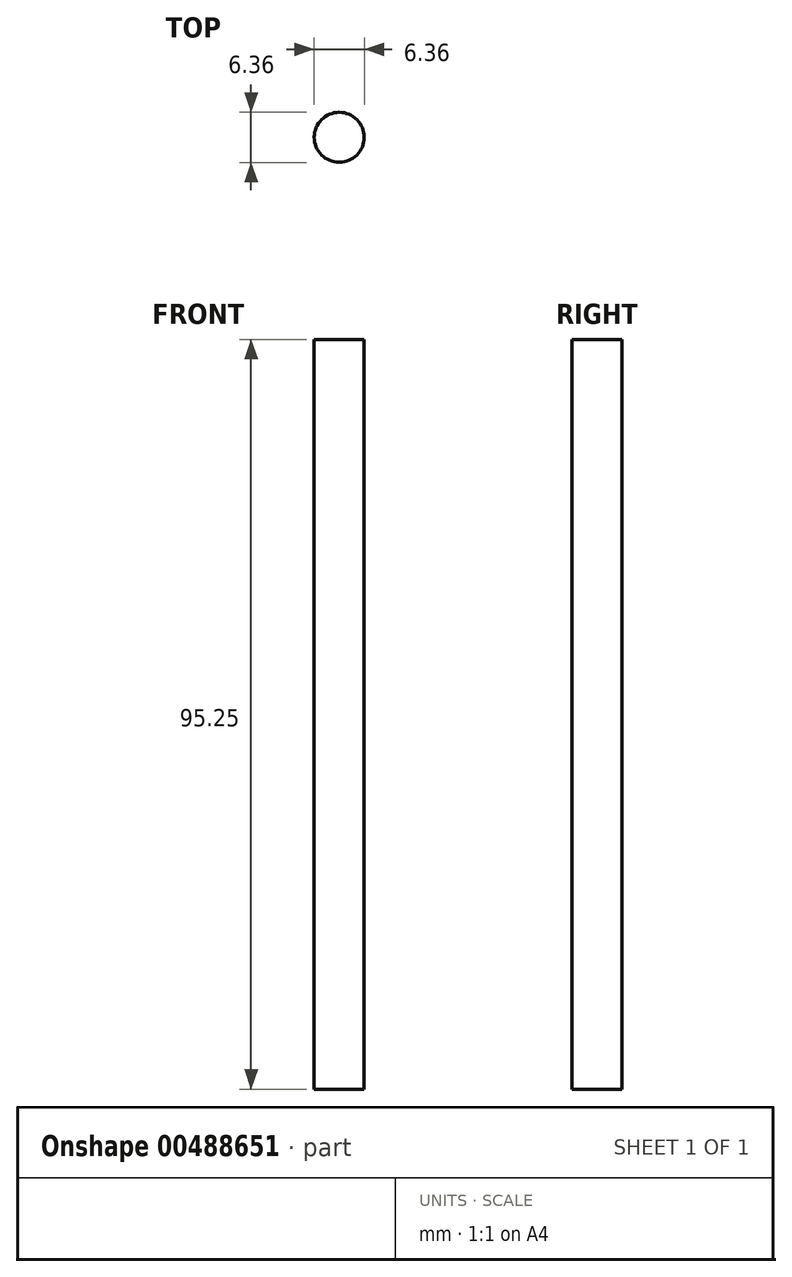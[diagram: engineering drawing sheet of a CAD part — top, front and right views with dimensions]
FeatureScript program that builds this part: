
annotation { "Feature Type Name" : "Feature", "Feature Type Description" : "" }
export const myFeature = defineFeature(function(context is Context, id is Id, definition is map)
    precondition{}
    {
        {
            var Q0;
            Q0=qCreatedBy(makeId("Top.planeOp"),FACE);
            var sketch = newSketch(context, id + "F0", { "sketchPlane" : qUnion([Q0])});
            skCircle(sketch, "E0", {"center": v(0, 0) * mm, "radius": 3.18 * mm});
            skSolve(sketch);
        }
        {
            var Q0;
            Q0=makeQuery(id+"F0.imprint","IMPRINT",FACE,{"disambiguationData":[TD([[makeQuery(id+"F0.imprint","IMPRINT",EDGE,{"derivedFrom":sQuery(id+"F0.wireOp",EDGE,"E0")}),1.0]])]});
            extrude(context, id + "F1", {"entities" : qUnion([Q0]), "depth" : 95.25 * mm});
        }
    });
